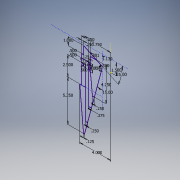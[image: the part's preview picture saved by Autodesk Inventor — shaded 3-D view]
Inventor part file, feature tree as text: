
AUTODESK INVENTOR PART (.ipt)
format: ipt  version: 2017 SP1 (Build 210196100, 196)  size: 122,880 bytes
history: native  units: in
note: dims shown in document units (in); Inventor stores cm internally (conversion verified against a paired STEP export)
features: sketch x1
ambient origin geometry x8: Origin, YZ Plane, XZ Plane, XY Plane, X Axis, Y Axis, Z Axis, Center Point
feature tree (1):
  sketch  "Sketch1"  dims[d0=0.5in d1=1.13in d3=15.0deg d4=0.25in d9=1.5in d11=0.5in d13=3.75in d14=0.25in d15=1.0in d16=0.25in d17=0.5in d18=0.234in d19=0.234in d20=0.5in d22=4.25in d23=2.5in d25=1.0in d26=0.25in d27=5.25in d28=0.125in d29=4.0in d30=0.25in d31=0.1718in d32=1.75in d33=0.125in d34=0.801in d35=0.375in]
